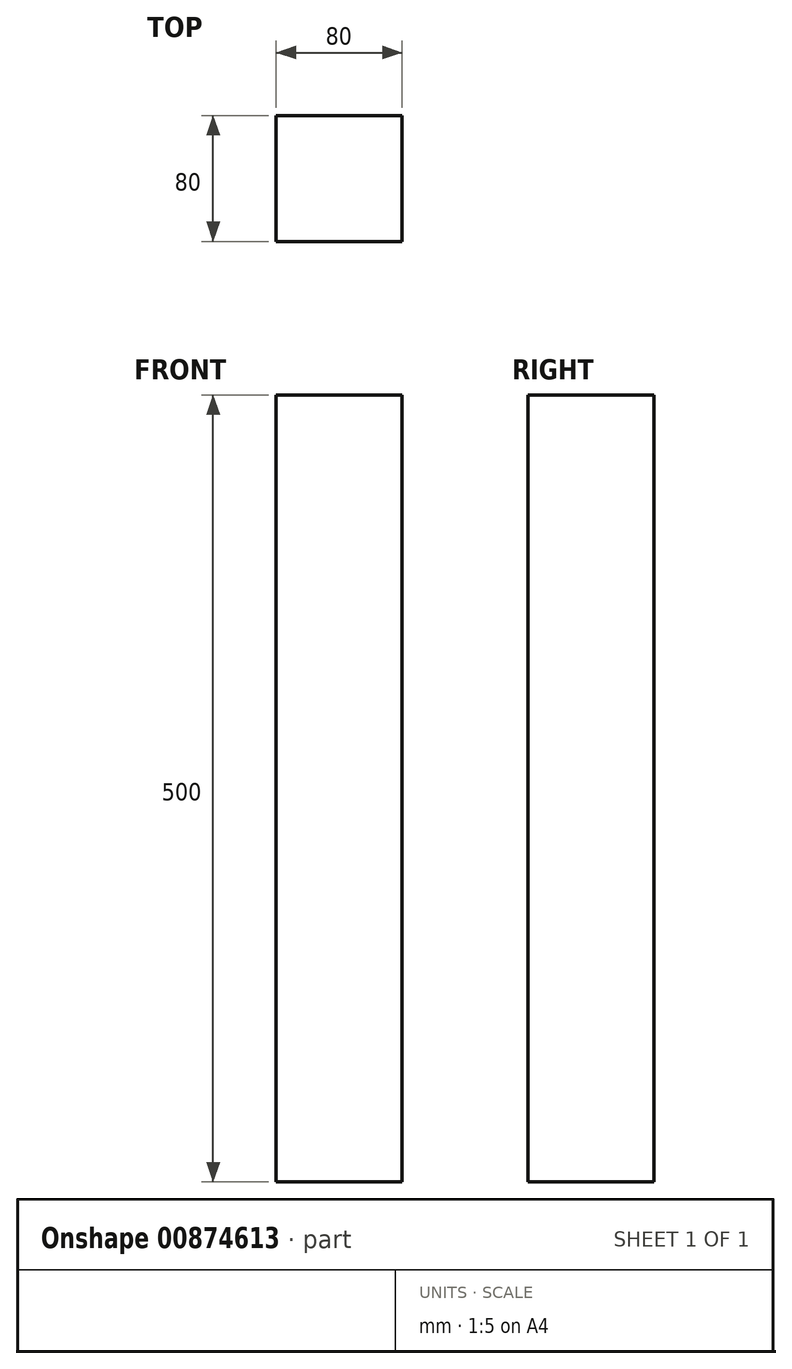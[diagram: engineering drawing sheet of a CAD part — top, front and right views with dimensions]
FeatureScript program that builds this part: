
annotation { "Feature Type Name" : "Feature", "Feature Type Description" : "" }
export const myFeature = defineFeature(function(context is Context, id is Id, definition is map)
    precondition{}
    {
        {
            var Q0;
            Q0=qCreatedBy(makeId("Top.planeOp"),FACE);
            var sketch = newSketch(context, id + "F0", { "sketchPlane" : qUnion([Q0])});
            skLineSegment(sketch, "E0.bottom", {"start": v(0, 0) * mm, "end": v(80, 0) * mm});
            skLineSegment(sketch, "E0.top", {"start": v(0, 80) * mm, "end": v(80, 80) * mm});
            skLineSegment(sketch, "E0.left", {"start": v(0, 0) * mm, "end": v(0, 80) * mm});
            skLineSegment(sketch, "E0.right", {"start": v(80, 0) * mm, "end": v(80, 80) * mm});
            skSolve(sketch);
        }
        {
            var Q0;
            Q0=makeQuery(id+"F0.imprint","IMPRINT",FACE,{"disambiguationData":[TD([[makeQuery(id+"F0.imprint","IMPRINT",EDGE,{"derivedFrom":sQuery(id+"F0.wireOp",EDGE,"E0.bottom")}),1.0]])]});
            extrude(context, id + "F1", {"entities" : qUnion([Q0]), "depth" : 500 * mm, "offsetDistance" : 25 * mm});
        }
    });
